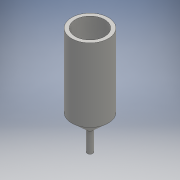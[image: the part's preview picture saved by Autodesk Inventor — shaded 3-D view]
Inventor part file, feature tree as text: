
AUTODESK INVENTOR PART (.ipt)
format: ipt  version: 2016 (Build 200138000, 138)  size: 107,520 bytes
history: native  units: mm
features: revolve x2, sketch x2, other x1, shell x1
ambient origin geometry x8: Origin, YZ Plane, XZ Plane, XY Plane, X Axis, Y Axis, Z Axis, Center Point
bodies: Body1 (feature_tree)
feature tree (6):
  other  "ソリッド1"
  revolve  "回転1"
  shell  "シェル1"  Thickness=80.0mm
  revolve  "回転2"
  sketch  "スケッチ1"
  sketch  "スケッチ2"
